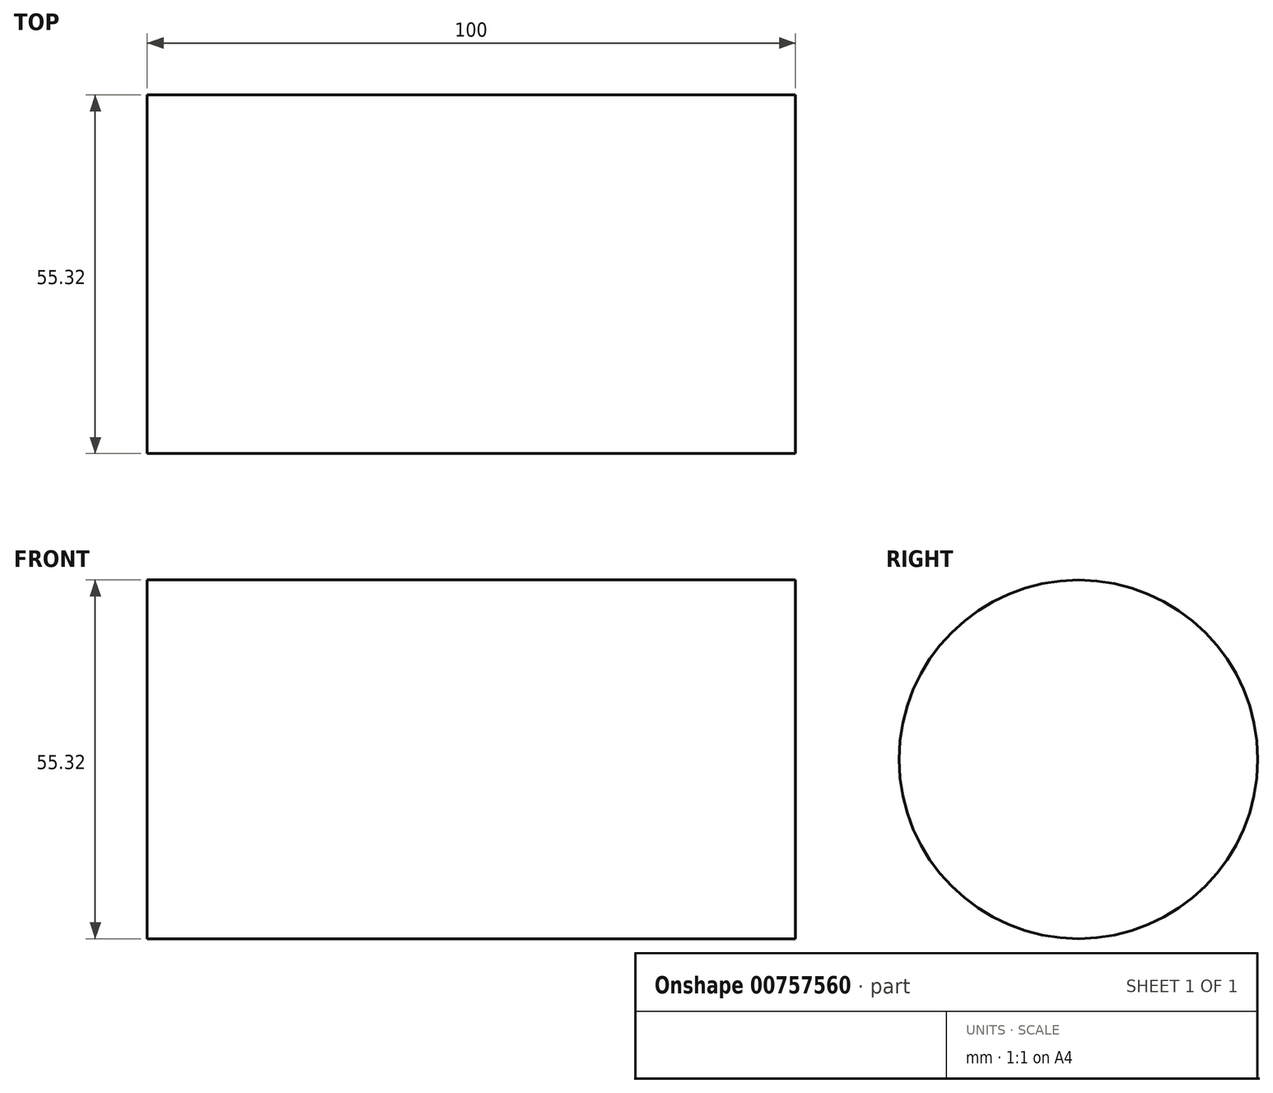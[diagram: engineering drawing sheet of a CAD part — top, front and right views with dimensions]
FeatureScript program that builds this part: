
annotation { "Feature Type Name" : "Feature", "Feature Type Description" : "" }
export const myFeature = defineFeature(function(context is Context, id is Id, definition is map)
    precondition{}
    {
        {
            var Q0;
            Q0=qCreatedBy(makeId("Right.planeOp"),FACE);
            var sketch = newSketch(context, id + "F0", { "sketchPlane" : qUnion([Q0])});
            skCircle(sketch, "E0", {"center": v(0, 0) * mm, "radius": 27.66 * mm});
            skSolve(sketch);
        }
        {
            var Q0;
            Q0 = qSketchRegion(id + "F0", true);
            var Q1;
            Q1=sQuery(id+"F0.wireOp",EDGE,"E0");
            extrude(context, id + "F1", {"entities" : qUnion([Q0]), "bodyType" : ToolBodyType.SURFACE, "surfaceEntities" : qUnion([Q1]), "endBound" : BoundingType.SYMMETRIC, "depth" : 100 * mm, "offsetDistance" : 25.4 * mm});
        }
    });
